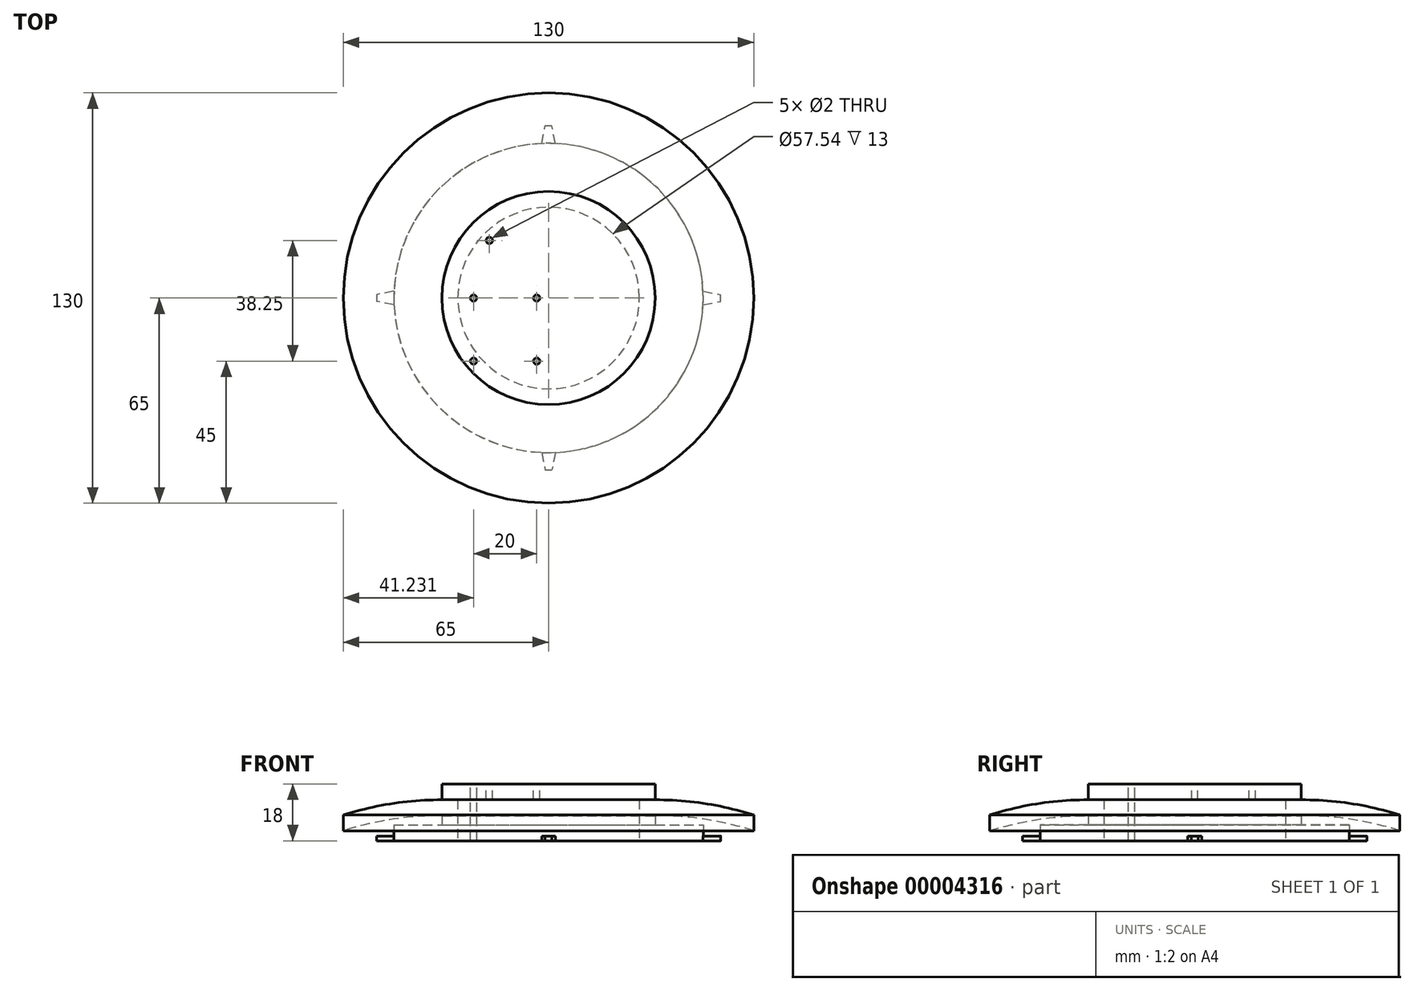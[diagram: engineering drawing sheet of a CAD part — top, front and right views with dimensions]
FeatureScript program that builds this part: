
annotation { "Feature Type Name" : "Feature", "Feature Type Description" : "" }
export const myFeature = defineFeature(function(context is Context, id is Id, definition is map)
    precondition{}
    {
        {
            var Q0;
            Q0=qCreatedBy(makeId("Front.planeOp"),FACE);
            var sketch = newSketch(context, id + "F0", { "sketchPlane" : qUnion([Q0])});
            skLineSegment(sketch, "E0", {"start": v(0, 0) * mm, "end": v(-50, 0) * mm});
            skLineSegment(sketch, "E1", {"start": v(-50, 0) * mm, "end": v(-55, 0) * mm});
            skLineSegment(sketch, "E2", {"start": v(0, 0) * mm, "end": v(0, 18) * mm});
            skLineSegment(sketch, "E3", {"start": v(-55, 1.5) * mm, "end": v(-55, 0) * mm});
            skLineSegment(sketch, "E4.0", {"start": v(0, 5) * mm, "end": v(-49, 5) * mm});
            skLineSegment(sketch, "E5.0", {"start": v(9.8, 8) * mm, "end": v(-33.77, 8) * mm});
            skLineSegment(sketch, "E6", {"start": v(-33.77, 8) * mm, "end": v(-33.77, 5) * mm});
            skArc(sketch, "E7.trimOffspring", {"start": v(-45.9, 5) * mm, "mid": v(-47.96, 3.99) * mm, "end": v(-50, 2.92) * mm, "construction": true});
            skLineSegment(sketch, "E8", {"start": v(0, 0) * mm, "end": v(55, 0) * mm});
            skLineSegment(sketch, "E9.0", {"start": v(0, 2) * mm, "end": v(55, 2) * mm});
            skLineSegment(sketch, "E10.0", {"start": v(0, 5) * mm, "end": v(55, 5) * mm});
            skLineSegment(sketch, "E11", {"start": v(0, 18) * mm, "end": v(65.62, 18) * mm});
            skLineSegment(sketch, "E12.0", {"start": v(0, -32) * mm, "end": v(65.62, -32) * mm});
            skLineSegment(sketch, "E13", {"start": v(0, 18) * mm, "end": v(-33.77, 18) * mm});
            skLineSegment(sketch, "E14", {"start": v(-33.77, 18) * mm, "end": v(-33.77, 13) * mm});
            skArc(sketch, "E15", {"start": v(-33.77, 8) * mm, "mid": v(-49.57, 6.79) * mm, "end": v(-65, 3.18) * mm});
            skLineSegment(sketch, "E16.0", {"start": v(4.8, 13) * mm, "end": v(-33.77, 13) * mm});
            skArc(sketch, "E17", {"start": v(-33.77, 13) * mm, "mid": v(-49.57, 11.79) * mm, "end": v(-65, 8.18) * mm});
            skLineSegment(sketch, "E18.0", {"start": v(-65, 8.18) * mm, "end": v(-65, 3.18) * mm});
            skLineSegment(sketch, "E19.0", {"start": v(-49, 1.5) * mm, "end": v(-55, 1.5) * mm});
            skLineSegment(sketch, "E20.0", {"start": v(-49, 5) * mm, "end": v(-49, 2.92) * mm});
            skLineSegment(sketch, "E21.0", {"start": v(-49, 1.5) * mm, "end": v(-49, 2.92) * mm});
            skSolve(sketch);
        }
        {
            var Q0;
            Q0=qCreatedBy(makeId("Top.planeOp"),FACE);
            var sketch = newSketch(context, id + "F1", { "sketchPlane" : qUnion([Q0])});
            skLineSegment(sketch, "E22.0", {"start": v(-50, 50) * mm, "end": v(-50, -50) * mm, "construction": true});
            skLineSegment(sketch, "E23.0", {"start": v(50, 50) * mm, "end": v(50, -50) * mm, "construction": true});
            skLineSegment(sketch, "E24.0", {"start": v(-50, -50) * mm, "end": v(50, -50) * mm, "construction": true});
            skLineSegment(sketch, "E25.0", {"start": v(-50, 50) * mm, "end": v(50, 50) * mm, "construction": true});
            skLineSegment(sketch, "E26.0", {"start": v(-5, 55) * mm, "end": v(-5, 49.75) * mm, "construction": true});
            skLineSegment(sketch, "E27.0", {"start": v(5, 55) * mm, "end": v(5, 49.75) * mm, "construction": true});
            skLineSegment(sketch, "E28.trimOffspring", {"start": v(-5, -49.75) * mm, "end": v(-5, -55) * mm, "construction": true});
            skLineSegment(sketch, "E29.trimOffspring", {"start": v(5, -49.75) * mm, "end": v(5, -55) * mm, "construction": true});
            skLineSegment(sketch, "E30.trimOffspring", {"start": v(49.75, 5) * mm, "end": v(55, 5) * mm, "construction": true});
            skLineSegment(sketch, "E31.0", {"start": v(-55, 55) * mm, "end": v(-55, -55) * mm, "construction": true});
            skLineSegment(sketch, "E32.0", {"start": v(-55, -55) * mm, "end": v(55, -55) * mm, "construction": true});
            skLineSegment(sketch, "E33.0", {"start": v(55, 55) * mm, "end": v(55, -55) * mm, "construction": true});
            skLineSegment(sketch, "E34.0", {"start": v(-55, 55) * mm, "end": v(55, 55) * mm, "construction": true});
            skLineSegment(sketch, "E35.0", {"start": v(-55, 0) * mm, "end": v(-50, 0) * mm, "construction": true});
            skCircle(sketch, "E36", {"center": v(0, 0) * mm, "radius": 55 * mm});
            skLineSegment(sketch, "E37.0", {"start": v(0, -50) * mm, "end": v(0, -55) * mm, "construction": true});
            skLineSegment(sketch, "E38.0", {"start": v(50, 0) * mm, "end": v(55, 0) * mm, "construction": true});
            skLineSegment(sketch, "E39.0", {"start": v(0, 55) * mm, "end": v(0, 50) * mm, "construction": true});
            skLineSegment(sketch, "E40.0", {"start": v(50, -1.5) * mm, "end": v(55, -1.5) * mm, "construction": true});
            skLineSegment(sketch, "E41.0", {"start": v(50, 1.5) * mm, "end": v(55, 1.5) * mm, "construction": true});
            skLineSegment(sketch, "E42.0", {"start": v(49.04, 2.5) * mm, "end": v(55, 2.5) * mm, "construction": true});
            skLineSegment(sketch, "E43.0", {"start": v(49.48, -2.5) * mm, "end": v(55, -2.5) * mm, "construction": true});
            skLineSegment(sketch, "E44.0", {"start": v(-1.5, -48.6) * mm, "end": v(-1.5, -55) * mm, "construction": true});
            skLineSegment(sketch, "E45.0", {"start": v(1.5, -48.4) * mm, "end": v(1.5, -55) * mm, "construction": true});
            skLineSegment(sketch, "E46.0", {"start": v(-2.5, -48.6) * mm, "end": v(-2.5, -55) * mm, "construction": true});
            skLineSegment(sketch, "E47.0", {"start": v(2.5, -48.4) * mm, "end": v(2.5, -55) * mm, "construction": true});
            skLineSegment(sketch, "E48.0", {"start": v(-1.5, 55) * mm, "end": v(-1.5, 49.02) * mm, "construction": true});
            skLineSegment(sketch, "E49.0", {"start": v(1.5, 55) * mm, "end": v(1.5, 49.18) * mm, "construction": true});
            skLineSegment(sketch, "E50.0", {"start": v(-2.5, 55) * mm, "end": v(-2.5, 49.16) * mm, "construction": true});
            skLineSegment(sketch, "E51.0", {"start": v(2.5, 55) * mm, "end": v(2.5, 49.11) * mm, "construction": true});
            skCircle(sketch, "E52.0", {"center": v(0, 0) * mm, "radius": 49 * mm});
            skLineSegment(sketch, "E53.0", {"start": v(48.07, 2.35) * mm, "end": v(54.9, 1) * mm});
            skLineSegment(sketch, "E54.0", {"start": v(48.37, -2.3) * mm, "end": v(54.9, -1) * mm});
            skLineSegment(sketch, "E55.0", {"start": v(2.26, -48.54) * mm, "end": v(1, -54.9) * mm});
            skLineSegment(sketch, "E56.0", {"start": v(-2.24, -48.62) * mm, "end": v(-1, -54.9) * mm});
            skLineSegment(sketch, "E57.0", {"start": v(-44.85, 3.01) * mm, "end": v(-54.9, 1) * mm});
            skLineSegment(sketch, "E58.0", {"start": v(-45.78, -2.8) * mm, "end": v(-54.9, -1) * mm});
            skLineSegment(sketch, "E59.0", {"start": v(2.28, 48.44) * mm, "end": v(1, 54.9) * mm});
            skLineSegment(sketch, "E60.0", {"start": v(-2.26, 48.53) * mm, "end": v(-1, 54.9) * mm});
            skCircle(sketch, "E61.0", {"center": v(0, 0) * mm, "radius": 54.5 * mm});
            skSolve(sketch);
        }
        {
            var Q0;
            {var subQ6=sQuery(id+"F0.wireOp",EDGE,"E0");Q0=makeQuery(id+"F0.imprint","IMPRINT",FACE,{"disambiguationData":[TD([[makeQuery(id+"F0.imprint","IMPRINT",EDGE,{"derivedFrom":subQ6}),-1.0]])]});}
            var Q1;
            {var subQ0=sQuery(id+"F0.wireOp",EDGE,"E6");Q1=makeQuery(id+"F0.imprint","IMPRINT",FACE,{"disambiguationData":[TD([[makeQuery(id+"F0.imprint","IMPRINT",EDGE,{"derivedFrom":subQ0}),1.0]])]});}
            var Q2;
            {var subQ3=sQuery(id+"F0.wireOp",EDGE,"4cf705f3-374d-4ae1-84bc-e01cbdcff2c7");Q2=makeQuery(id+"F0.imprint","IMPRINT",FACE,{"disambiguationData":[TD([[makeQuery(id+"F0.imprint","IMPRINT",EDGE,{"derivedFrom":subQ3}),1.0]])]});}
            var Q3;
            {var subQ4=sQuery(id+"F0.wireOp",EDGE,"E13");Q3=makeQuery(id+"F0.imprint","IMPRINT",FACE,{"disambiguationData":[TD([[makeQuery(id+"F0.imprint","IMPRINT",EDGE,{"derivedFrom":subQ4}),1.0]])]});}
            var Q4;
            Q4=makeQuery(id+"F0.imprint","IMPRINT",FACE,{"disambiguationData":[TD([[makeQuery(id+"F0.imprint","IMPRINT",EDGE,{"derivedFrom":sQuery(id+"F0.wireOp",EDGE,"293a7503-be2f-4d31-9126-d1959f43df71")}),1.0]])]});
            var Q5;
            {var subQ4=sQuery(id+"F0.wireOp",EDGE,"E15");Q5=makeQuery(id+"F0.imprint","IMPRINT",FACE,{"disambiguationData":[TD([[makeQuery(id+"F0.imprint","IMPRINT",EDGE,{"derivedFrom":subQ4}),-1.0]])]});}
            var Q6;
            Q6=sQuery(id+"F0.wireOp",EDGE,"E2");
            revolve(context, id + "F2", {"entities" : qUnion([Q0, Q1, Q2, Q3, Q4, Q5]), "axis" : qUnion([Q6]), "revolveType" : RevolveType.FULL});
        }
        {
            var Q0;
            {var subQ1=sQuery(id+"F1.wireOp",EDGE,"E58.0");var subQ5=sQuery(id+"F1.wireOp",EDGE,"E52.0");var subQ6=makeQuery(id+"F1.imprint","INTERSECT",VERTEX,{"derivedFrom":[subQ5,subQ1]});Q0=makeQuery(id+"F1.imprint","IMPRINT",FACE,{"disambiguationData":[TD([[makeQuery(id+"F1.imprint","IMPRINT",EDGE,{"disambiguationData":[TD([[subQ6,-1.0]])],"derivedFrom":subQ5}),-1.0]])]});}
            var Q1;
            {var subQ1=sQuery(id+"F1.wireOp",EDGE,"E60.0");var subQ5=sQuery(id+"F1.wireOp",EDGE,"E52.0");var subQ6=makeQuery(id+"F1.imprint","INTERSECT",VERTEX,{"derivedFrom":[subQ5,subQ1]});Q1=makeQuery(id+"F1.imprint","IMPRINT",FACE,{"disambiguationData":[TD([[makeQuery(id+"F1.imprint","IMPRINT",EDGE,{"disambiguationData":[TD([[subQ6,-1.0]])],"derivedFrom":subQ5}),-1.0]])]});}
            var Q2;
            {var subQ1=sQuery(id+"F1.wireOp",EDGE,"E59.0");var subQ5=sQuery(id+"F1.wireOp",EDGE,"E52.0");var subQ6=makeQuery(id+"F1.imprint","INTERSECT",VERTEX,{"derivedFrom":[subQ5,subQ1]});Q2=makeQuery(id+"F1.imprint","IMPRINT",FACE,{"disambiguationData":[TD([[makeQuery(id+"F1.imprint","IMPRINT",EDGE,{"disambiguationData":[TD([[subQ6,1.0]])],"derivedFrom":subQ5}),-1.0]])]});}
            var Q3;
            {var subQ1=sQuery(id+"F1.wireOp",EDGE,"E55.0");var subQ5=sQuery(id+"F1.wireOp",EDGE,"E52.0");var subQ6=makeQuery(id+"F1.imprint","INTERSECT",VERTEX,{"derivedFrom":[subQ5,subQ1]});Q3=makeQuery(id+"F1.imprint","IMPRINT",FACE,{"disambiguationData":[TD([[makeQuery(id+"F1.imprint","IMPRINT",EDGE,{"disambiguationData":[TD([[subQ6,-1.0]])],"derivedFrom":subQ5}),-1.0]])]});}
            var Q4;
            Q4=makeQuery(id+"F1.imprint","IMPRINT",FACE,{"disambiguationData":[TD([[makeQuery(id+"F1.imprint","IMPRINT",EDGE,{"derivedFrom":sQuery(id+"F1.wireOp",EDGE,"E36")}),1.0]])]});
            extrude(context, id + "F3", {"entities" : qUnion([Q0, Q1, Q2, Q3, Q4]), "operationType" : NewBodyOperationType.REMOVE, "depth" : 2 * mm});
        }
        {
            var Q0;
            Q0=makeQuery(id+"F2.opRevolve","SWEPT_FACE",FACE,{"disambiguationData":[OSD([sQuery(id+"F0.wireOp",EDGE,"E0"),sQuery(id+"F0.wireOp",EDGE,"E1")])]});
            shell(context, id + "F4", {"entities" : qUnion([Q0]), "thickness" : 5 * mm});
        }
        {
            var Q0;
            Q0=makeQuery(id+"F2.opRevolve","SWEPT_FACE",FACE,{"disambiguationData":[OSD([sQuery(id+"F0.wireOp",EDGE,"E13")])]});
            var sketch = newSketch(context, id + "F5", { "sketchPlane" : qUnion([Q0])});
            skLineSegment(sketch, "E62", {"start": v(-3.77, 0) * mm, "end": v(-23.77, 0) * mm});
            skLineSegment(sketch, "E63", {"start": v(-33.77, 0) * mm, "end": v(-33.77, -20) * mm});
            skLineSegment(sketch, "E64.0", {"start": v(-23.77, 0) * mm, "end": v(-23.77, -20) * mm});
            skLineSegment(sketch, "E65.0", {"start": v(-3.77, 0) * mm, "end": v(-3.77, -20) * mm});
            skLineSegment(sketch, "E66", {"start": v(-3.77, -20) * mm, "end": v(-23.77, -20) * mm});
            skCircle(sketch, "E67", {"center": v(-23.77, -20) * mm, "radius": 1 * mm});
            skCircle(sketch, "E68", {"center": v(-3.77, -20) * mm, "radius": 1 * mm});
            skCircle(sketch, "E69", {"center": v(-23.77, 0) * mm, "radius": 1 * mm});
            skCircle(sketch, "E70", {"center": v(-3.77, 0) * mm, "radius": 1 * mm});
            skLineSegment(sketch, "E71.0", {"start": v(-18.77, 0) * mm, "end": v(-18.77, 18.25) * mm});
            skCircle(sketch, "E72", {"center": v(-18.77, 18.25) * mm, "radius": 1 * mm});
            skSolve(sketch);
        }
        {
            var Q0;
            {var subQ1=sQuery(id+"F5.wireOp",EDGE,"E64.0");var subQ3=sQuery(id+"F5.wireOp",EDGE,"E62");var subQ5=makeQuery(id+"F5.imprint","INTERSECT",VERTEX,{"derivedFrom":[subQ3,subQ1]});Q0=makeQuery(id+"F5.imprint","IMPRINT",FACE,{"disambiguationData":[TD([[makeQuery(id+"F5.imprint","IMPRINT",EDGE,{"disambiguationData":[TD([[subQ5,1.0]])],"derivedFrom":subQ3}),-1.0]])]});}
            var Q1;
            {var subQ1=sQuery(id+"F5.wireOp",EDGE,"E64.0");var subQ3=sQuery(id+"F5.wireOp",EDGE,"E62");var subQ5=makeQuery(id+"F5.imprint","INTERSECT",VERTEX,{"derivedFrom":[subQ3,subQ1]});Q1=makeQuery(id+"F5.imprint","IMPRINT",FACE,{"disambiguationData":[TD([[makeQuery(id+"F5.imprint","IMPRINT",EDGE,{"disambiguationData":[TD([[subQ5,1.0]])],"derivedFrom":subQ3}),1.0]])]});}
            var Q2;
            {var subQ1=sQuery(id+"F5.wireOp",EDGE,"E66");var subQ3=sQuery(id+"F5.wireOp",EDGE,"E64.0");var subQ5=makeQuery(id+"F5.imprint","INTERSECT",VERTEX,{"derivedFrom":[subQ3,subQ1]});Q2=makeQuery(id+"F5.imprint","IMPRINT",FACE,{"disambiguationData":[TD([[makeQuery(id+"F5.imprint","IMPRINT",EDGE,{"disambiguationData":[TD([[subQ5,1.0]])],"derivedFrom":subQ3}),-1.0]])]});}
            var Q3;
            {var subQ1=sQuery(id+"F5.wireOp",EDGE,"E66");var subQ3=sQuery(id+"F5.wireOp",EDGE,"E64.0");var subQ5=makeQuery(id+"F5.imprint","INTERSECT",VERTEX,{"derivedFrom":[subQ3,subQ1]});Q3=makeQuery(id+"F5.imprint","IMPRINT",FACE,{"disambiguationData":[TD([[makeQuery(id+"F5.imprint","IMPRINT",EDGE,{"disambiguationData":[TD([[subQ5,1.0]])],"derivedFrom":subQ3}),1.0]])]});}
            var Q4;
            {var subQ1=sQuery(id+"F5.wireOp",EDGE,"E66");var subQ3=sQuery(id+"F5.wireOp",EDGE,"E65.0");var subQ5=makeQuery(id+"F5.imprint","INTERSECT",VERTEX,{"derivedFrom":[subQ3,subQ1]});Q4=makeQuery(id+"F5.imprint","IMPRINT",FACE,{"disambiguationData":[TD([[makeQuery(id+"F5.imprint","IMPRINT",EDGE,{"disambiguationData":[TD([[subQ5,1.0]])],"derivedFrom":subQ3}),1.0]])]});}
            var Q5;
            {var subQ1=sQuery(id+"F5.wireOp",EDGE,"E66");var subQ3=sQuery(id+"F5.wireOp",EDGE,"E65.0");var subQ5=makeQuery(id+"F5.imprint","INTERSECT",VERTEX,{"derivedFrom":[subQ3,subQ1]});Q5=makeQuery(id+"F5.imprint","IMPRINT",FACE,{"disambiguationData":[TD([[makeQuery(id+"F5.imprint","IMPRINT",EDGE,{"disambiguationData":[TD([[subQ5,1.0]])],"derivedFrom":subQ3}),-1.0]])]});}
            var Q6;
            {var subQ1=sQuery(id+"F5.wireOp",EDGE,"E65.0");var subQ3=sQuery(id+"F5.wireOp",EDGE,"E62");var subQ5=makeQuery(id+"F5.imprint","INTERSECT",VERTEX,{"derivedFrom":[subQ3,subQ1]});Q6=makeQuery(id+"F5.imprint","IMPRINT",FACE,{"disambiguationData":[TD([[makeQuery(id+"F5.imprint","IMPRINT",EDGE,{"disambiguationData":[TD([[subQ5,-1.0]])],"derivedFrom":subQ3}),-1.0]])]});}
            var Q7;
            {var subQ1=sQuery(id+"F5.wireOp",EDGE,"E65.0");var subQ3=sQuery(id+"F5.wireOp",EDGE,"E62");var subQ5=makeQuery(id+"F5.imprint","INTERSECT",VERTEX,{"derivedFrom":[subQ3,subQ1]});Q7=makeQuery(id+"F5.imprint","IMPRINT",FACE,{"disambiguationData":[TD([[makeQuery(id+"F5.imprint","IMPRINT",EDGE,{"disambiguationData":[TD([[subQ5,-1.0]])],"derivedFrom":subQ3}),1.0]])]});}
            var Q8;
            Q8=makeQuery(id+"F5.imprint","IMPRINT",FACE,{"disambiguationData":[TD([[makeQuery(id+"F5.imprint","IMPRINT",EDGE,{"derivedFrom":sQuery(id+"F5.wireOp",EDGE,"E72")}),1.0]])]});
            extrude(context, id + "F6", {"entities" : qUnion([Q0, Q1, Q2, Q3, Q4, Q5, Q6, Q7, Q8]), "operationType" : NewBodyOperationType.REMOVE, "oppositeDirection" : true, "depth" : 25 * mm});
        }
    });
